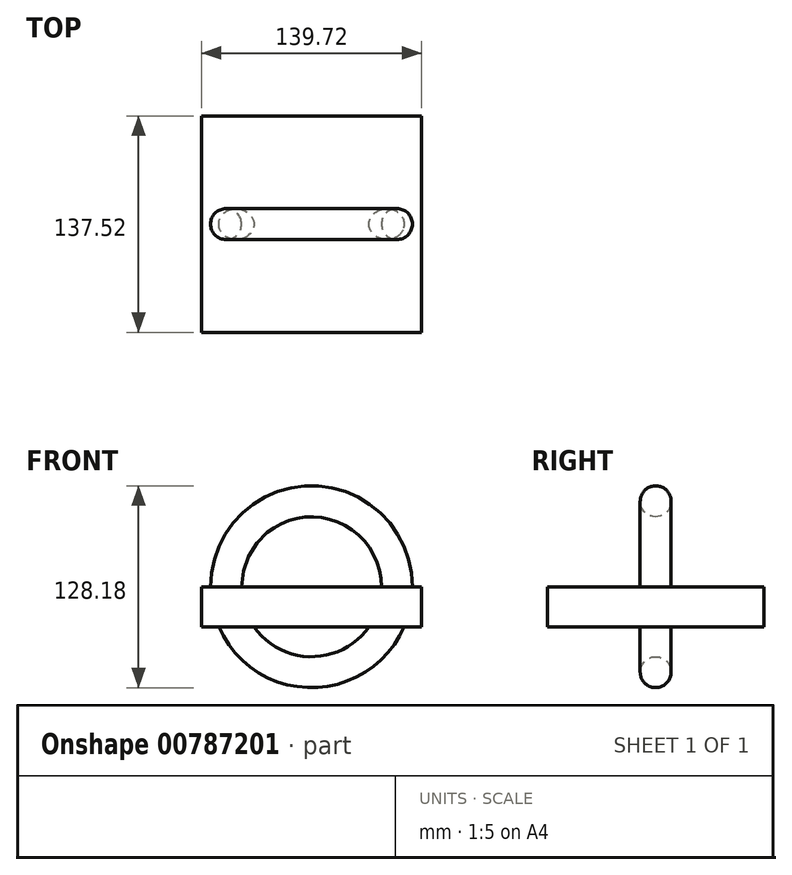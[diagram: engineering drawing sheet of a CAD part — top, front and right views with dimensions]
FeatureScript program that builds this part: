
annotation { "Feature Type Name" : "Feature", "Feature Type Description" : "" }
export const myFeature = defineFeature(function(context is Context, id is Id, definition is map)
    precondition{}
    {
        {
            var Q0;
            Q0=qCreatedBy(makeId("Top.planeOp"),FACE);
            var sketch = newSketch(context, id + "F0", { "sketchPlane" : qUnion([Q0])});
            skLineSegment(sketch, "E0.bottom", {"start": v(69.86, -68.76) * mm, "end": v(-69.86, -68.76) * mm});
            skLineSegment(sketch, "E0.top", {"start": v(69.86, 68.76) * mm, "end": v(-69.86, 68.76) * mm});
            skLineSegment(sketch, "E0.left", {"start": v(69.86, -68.76) * mm, "end": v(69.86, 68.76) * mm});
            skLineSegment(sketch, "E0.right", {"start": v(-69.86, -68.76) * mm, "end": v(-69.86, 68.76) * mm});
            skPoint(sketch, "E0.middle", {"position": v(0, 0) * mm});
            skLineSegment(sketch, "E1", {"start": v(0, 68.76) * mm, "end": v(0, -68.76) * mm});
            skSolve(sketch);
        }
        {
            var Q0;
            Q0=qCreatedBy(makeId("Top.planeOp"),FACE);
            var sketch = newSketch(context, id + "F1", { "sketchPlane" : qUnion([Q0])});
            skCircle(sketch, "E2", {"center": v(54.26, 0) * mm, "radius": 9.82 * mm});
            skSolve(sketch);
        }
        {
            var Q0;
            {var subQ0=sQuery(id+"F0.wireOp",EDGE,"E0.right");Q0=makeQuery(id+"F0.imprint","IMPRINT",FACE,{"disambiguationData":[TD([[makeQuery(id+"F0.imprint","IMPRINT",EDGE,{"derivedFrom":subQ0}),-1.0]])]});}
            var Q1;
            {var subQ0=sQuery(id+"F0.wireOp",EDGE,"E0.left");Q1=makeQuery(id+"F0.imprint","IMPRINT",FACE,{"disambiguationData":[TD([[makeQuery(id+"F0.imprint","IMPRINT",EDGE,{"derivedFrom":subQ0}),1.0]])]});}
            extrude(context, id + "F2", {"entities" : qUnion([Q0, Q1]), "depth" : -25.4 * mm, "offsetDistance" : 25.4 * mm});
        }
        {
            var Q0;
            Q0=makeQuery(id+"F1.imprint","IMPRINT",FACE,{"disambiguationData":[TD([[makeQuery(id+"F1.imprint","IMPRINT",EDGE,{"derivedFrom":sQuery(id+"F1.wireOp",EDGE,"E2")}),1.0]])]});
            var Q1;
            Q1=sQuery(id+"F0.wireOp",EDGE,"E1");
            revolve(context, id + "F3", {"operationType" : NewBodyOperationType.ADD, "surfaceOperationType" : NewSurfaceOperationType.NEW, "entities" : qUnion([Q0]), "axis" : qUnion([Q1]), "revolveType" : RevolveType.FULL});
        }
    });
